# Revit family: Countertop-Supports_Centerline-Brackets_Commercial-Standard-Bracket
name_source: partatom
category: Casework
units: mm (PartAtom-declared; Revit-internal decimal feet)

## family parameters
Always vertical = Yes
Cut with Voids When Loaded = No
OmniClass Number = 23.40.35.11
OmniClass Title = Casework Components
Room Calculation Point = No
Shared = No
Work Plane-Based = No

## types (4) — shared parameters
Assembly Code = E2010200
Default Elevation = 0"
Depth = 3 1/2"
Description = Commercial Standard Bracket
Finish = Available Powder Coat Finishes; White (W), Black (B)
Finish Note = When choosing an alternative finish, please remember to update the model number to reflect the chosen finish.
Height = 1/2"
Keynote = 12000
Manufacturer = Centerline Brackets
Product Material = Centerline Brackets - Steel - Powder Coated - Black (B)
Product data url = https://www.bimobject.com
URL = https://www.countertopbracket.com

## per-type parameters (varying)
| type | Model |
| 8" | CST-08 |
| 10" | CST-10 |
| 12" | CST-12 |
| 14" | CST-14 |

note: column(s) folded — value = type name in every type: Length

## geometry (parser evidence)
native form markers: Sweep x4
no freeform markers — native parametric forms only
